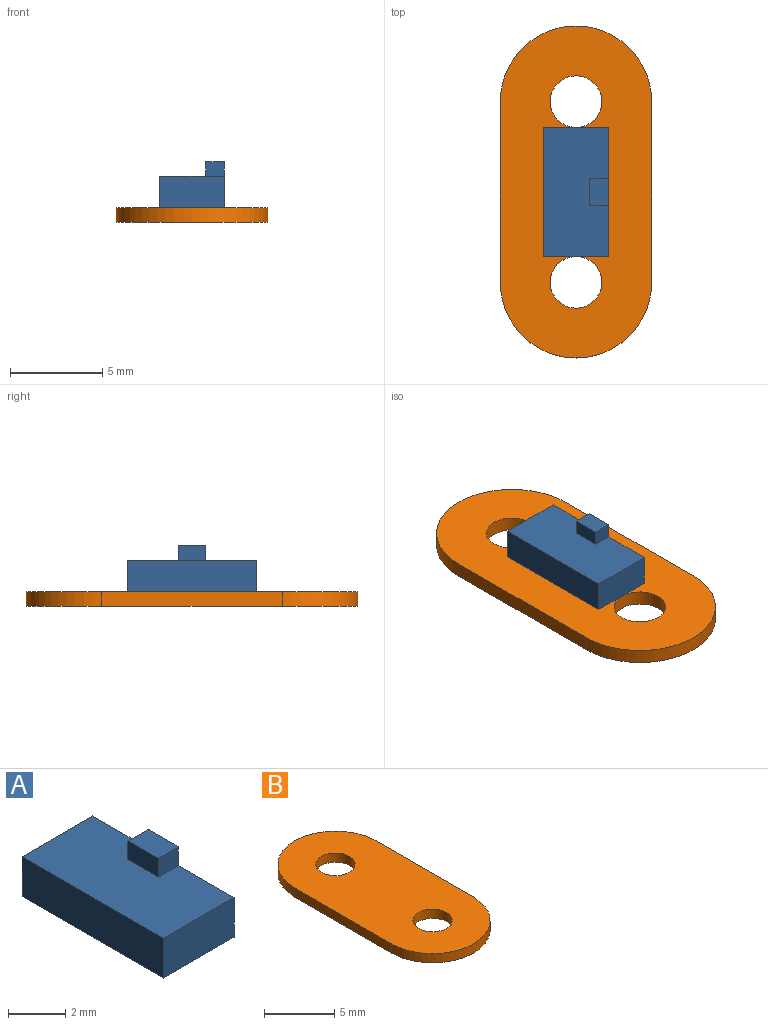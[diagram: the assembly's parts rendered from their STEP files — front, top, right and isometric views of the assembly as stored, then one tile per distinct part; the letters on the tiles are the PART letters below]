
ASSEMBLY  parts=2 mates=1
PART A: 10 faces, bbox 3.5x7x2.5 mm
  f0: plane 7x2.5mm, normal (1,0,0), area 13.1mm2, adj f1,f3,f4,f5,f6,f8,f9
  f1: plane 3.5x1.7mm, normal (0,1,0), area 5.9mm2, adj f0,f2,f4,f5
  f2: plane 7x1.7mm, normal (-1,0,0), area 11.9mm2, adj f1,f3,f4,f5
  f3: plane 3.5x1.7mm, normal (0,-1,0), area 5.9mm2, adj f0,f2,f4,f5
  f4: plane 7x3.5mm, normal (0,0,1), area 23mm2, adj f0,f1,f2,f3,f6,f7,f8
  f5: plane 7x3.5mm, normal (0,0,-1), area 24.5mm2, adj f0,f1,f2,f3
  f6: plane 1x0.8mm, normal (0,1,0), area 0.8mm2, adj f0,f4,f7,f9
  f7: plane 1.5x0.8mm, normal (-1,0,0), area 1.2mm2, adj f4,f6,f8,f9
  f8: plane 1x0.8mm, normal (0,-1,0), area 0.8mm2, adj f0,f4,f7,f9
  f9: plane 1.5x1mm, normal (0,0,1), area 1.5mm2, adj f0,f6,f7,f8
PART B: 8 faces, bbox 8.2x18x0.8 mm
  f0: plane 9.8x0.8mm, normal (1,0,0), area 7.8mm2, adj f1,f5,f6,f7
  f1: cylinder r=4.1mm len=8.2mm, axis (0,0,-1), area 10.3mm2, adj f0,f2,f6,f7
  f2: plane 9.8x0.8mm, normal (-1,0,0), area 7.8mm2, adj f1,f5,f6,f7
  f3: cylinder r=1.4mm len=2.8mm, axis (0,0,-1), area 7mm2, adj f6,f7
  f4: cylinder r=1.4mm len=2.8mm, axis (0,0,-1), area 7mm2, adj f6,f7
  f5: cylinder r=4.1mm len=8.2mm, axis (0,0,-1), area 10.3mm2, adj f0,f2,f6,f7
  f6: plane 18x8.2mm, normal (0,0,1), area 120.9mm2, adj f0,f1,f2,f3,f4,f5
  f7: plane 18x8.2mm, normal (0,0,-1), area 120.9mm2, adj f0,f1,f2,f3,f4,f5
PLACE A t=(-14.42,-26.58,10.2)mm
PLACE B t=(3.55,-24,9.4)mm
MATE fastened A.f5 <-> B.f6  axis (0,0,-1) through (-26.41,-3.64,10.2)mm
